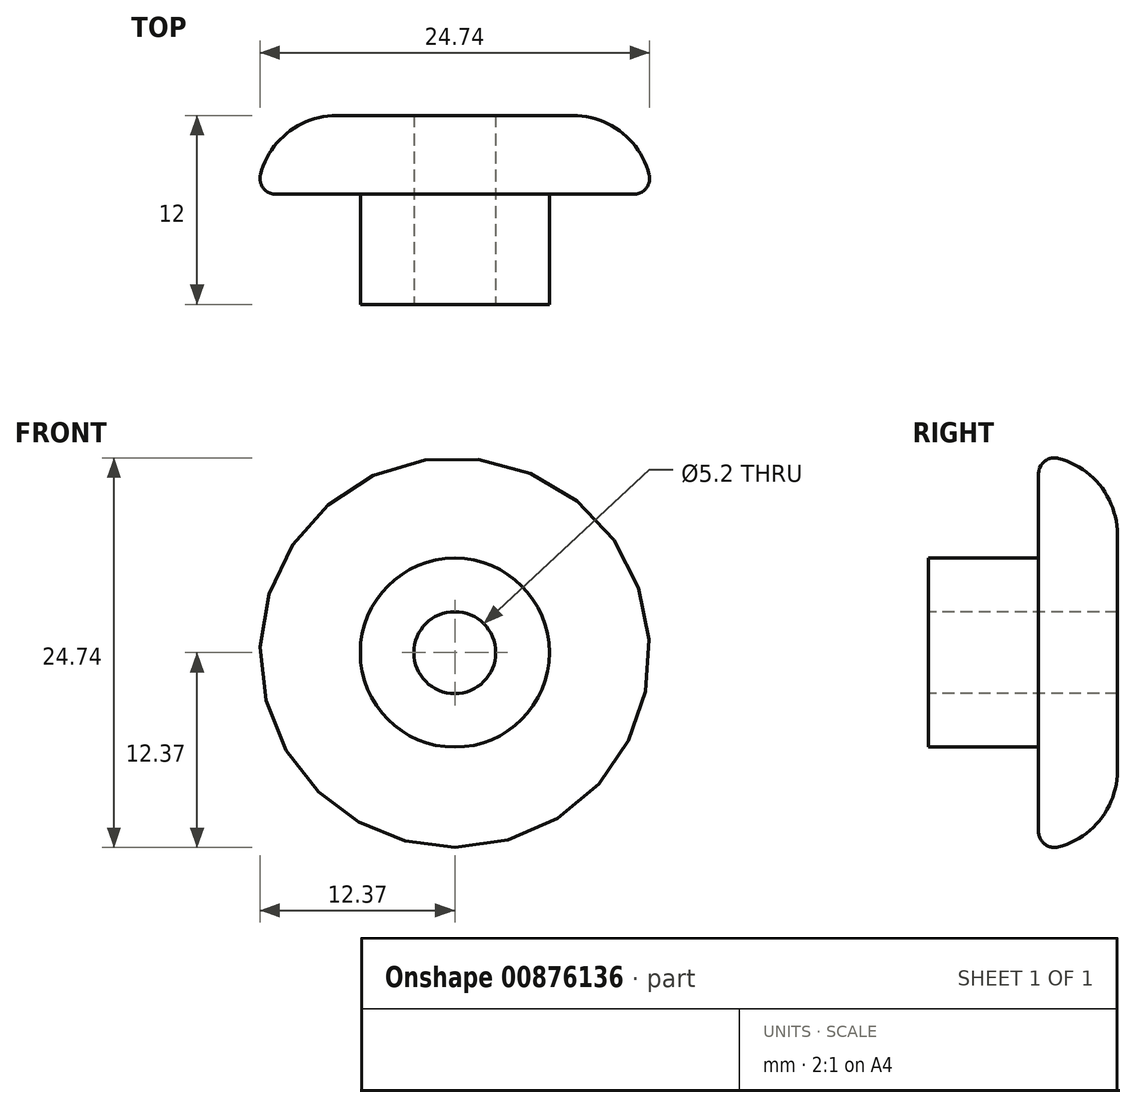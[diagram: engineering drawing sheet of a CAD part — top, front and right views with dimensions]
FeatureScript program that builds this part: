
annotation { "Feature Type Name" : "Feature", "Feature Type Description" : "" }
export const myFeature = defineFeature(function(context is Context, id is Id, definition is map)
    precondition{}
    {
        {
            var Q0;
            Q0=qCreatedBy(makeId("Front.planeOp"),FACE);
            var sketch = newSketch(context, id + "F0", { "sketchPlane" : qUnion([Q0])});
            skCircle(sketch, "E0", {"center": v(0, 0) * mm, "radius": 12.5 * mm});
            skSolve(sketch);
        }
        {
            var Q0;
            Q0=makeQuery(id+"F0.imprint","IMPRINT",FACE,{"disambiguationData":[TD([[makeQuery(id+"F0.imprint","IMPRINT",EDGE,{"derivedFrom":sQuery(id+"F0.wireOp",EDGE,"E0")}),1.0]])]});
            extrude(context, id + "F1", {"entities" : qUnion([Q0]), "depth" : 5 * mm, "offsetDistance" : 25 * mm});
        }
        {
            var Q0;
            Q0=makeQuery(id+"F1.opExtrude","CAP_EDGE",EDGE,{"disambiguationData":[OSD([sQuery(id+"F0.wireOp",EDGE,"E0")])],"isStart":true});
            fillet(context, id + "F2", {"entities" : qUnion([Q0]), "radius" : 5 * mm, "tangentPropagation" : true, "allowEdgeOverflow" : false});
        }
        {
            var Q0;
            Q0=makeQuery(id+"F1.opExtrude","CAP_FACE",FACE,{"disambiguationData":[OSD([sQuery(id+"F0.wireOp",EDGE,"E0")])],"isStart":false});
            var sketch = newSketch(context, id + "F3", { "sketchPlane" : qUnion([Q0])});
            skCircle(sketch, "E1", {"center": v(0, 0) * mm, "radius": 6 * mm});
            skSolve(sketch);
        }
        {
            var Q0;
            Q0=makeQuery(id+"F3.imprint","IMPRINT",FACE,{"disambiguationData":[TD([[makeQuery(id+"F3.imprint","IMPRINT",EDGE,{"derivedFrom":sQuery(id+"F3.wireOp",EDGE,"E1")}),1.0]])]});
            extrude(context, id + "F4", {"entities" : qUnion([Q0]), "operationType" : NewBodyOperationType.ADD, "depth" : 7 * mm, "offsetDistance" : 25 * mm});
        }
        {
            var Q0;
            {var subQ0=sQuery(id+"F0.wireOp",EDGE,"E0");Q0=makeQuery(id+"F2.opFillet","BLEND_EDGE",EDGE,{"blendedFrom":[makeQuery(id+"F1.opExtrude","CAP_EDGE",EDGE,{"disambiguationData":[OSD([subQ0])],"isStart":true}),makeQuery(id+"F1.opExtrude","CAP_FACE",FACE,{"disambiguationData":[OSD([subQ0])],"isStart":false})],"blendedInto":[makeQuery(id+"F1.opExtrude","CAP_FACE",FACE,{"disambiguationData":[OSD([subQ0])],"isStart":false})]});}
            fillet(context, id + "F5", {"entities" : qUnion([Q0]), "radius" : 1 * mm, "tangentPropagation" : true, "allowEdgeOverflow" : false});
        }
        {
            var Q0;
            Q0=makeQuery(id+"F4.opExtrude","CAP_FACE",FACE,{"disambiguationData":[OSD([sQuery(id+"F3.wireOp",EDGE,"E1")])],"isStart":false});
            var sketch = newSketch(context, id + "F6", { "sketchPlane" : qUnion([Q0])});
            skCircle(sketch, "E2", {"center": v(0, 0) * mm, "radius": 2.6 * mm});
            skSolve(sketch);
        }
        {
            var Q0;
            Q0=makeQuery(id+"F6.imprint","IMPRINT",FACE,{"disambiguationData":[TD([[makeQuery(id+"F6.imprint","IMPRINT",EDGE,{"derivedFrom":sQuery(id+"F6.wireOp",EDGE,"E2")}),1.0]])]});
            extrude(context, id + "F7", {"entities" : qUnion([Q0]), "operationType" : NewBodyOperationType.REMOVE, "oppositeDirection" : true, "depth" : 25 * mm, "offsetDistance" : 25 * mm});
        }
    });
